# Revit family: Deca_Chuveiro Redondo de Parede_Flex Plus_2083.STD
name_source: partatom
category: Plumbing Fixtures
units: mm (PartAtom-declared; Revit-internal decimal feet)

## family parameters
Cut with Voids When Loaded = No
Host = Face
Part Type = Normal
Room Calculation Point = No
Round Connector Dimension = Use Radius
Shared = No

## types (1)
- 2083.C.STD_Cromado
    Acompanha o Produto = RESTRITOR DE VAZÃO
    Aprovado por = quattroD
    Atendimento ao Cliente = 0800 011 7073
    Categoria = CHUVEIROS E DUCHAS
    Composição Anel Vedação = -
    Composição Assento = -
    Composição Básica = Liga de Cobre (bronze e latão),Plásticos de Engenharia,Elastômeros
    Composição Componente = -
    Consumo = -
    Cor Interna = -
    Cor Principal = Cromado
    Cor Secundária = Preto
    Cores Componente = -
    Criado por = quattroD
    Código Pai = 2083.C.STD
    Default Elevation = 2.2 m
    Description = CHUVEIRO REDONDO PAREDE CR (160mm)
    Diâmetro Água Fria = 0.02 m
    HWFU = 0
    Informações Complementares = -
    Itens de Instalação = -
    Linha = Flex
    Manufacturer = Deca
    Material = Deca_Cromado
    Material secundário = Deca_Preto
    Model = 2083.C.STD
    Norma = NBR 15206
    Peso Líquido (Kg) = 0.56
    Pressão mín. Aquec. Acúmulo = 4 MCA
    Pressão mín. Aquec. Passagem = 8 MCA
    Raio Água Fria = 0.01 m
    Saída de Esgoto = -
    Segmento = -
    Tipo de dispositivo economizador = RESTRITOR VAZÃO DE 12L/MIN
    Tipo de mecanismo utilizado = -
    Tipo de rosca de entrada = BSP NBR 8133
    Tipo de rosca de saída = -
    URL = www.deca.com.br
    Vazão na Pressão máx. (L/min) = 30
    Vazão na Pressão mín. (L/min) = 6

note: source unit labels omitted for Vazão na Pressão máx. (L/min), Vazão na Pressão mín. (L/min) — the stored unit's dimension contradicts the parameter name (converter mislabeling)

## geometry (parser evidence)
native form markers: Sweep x2
no freeform markers — native parametric forms only
